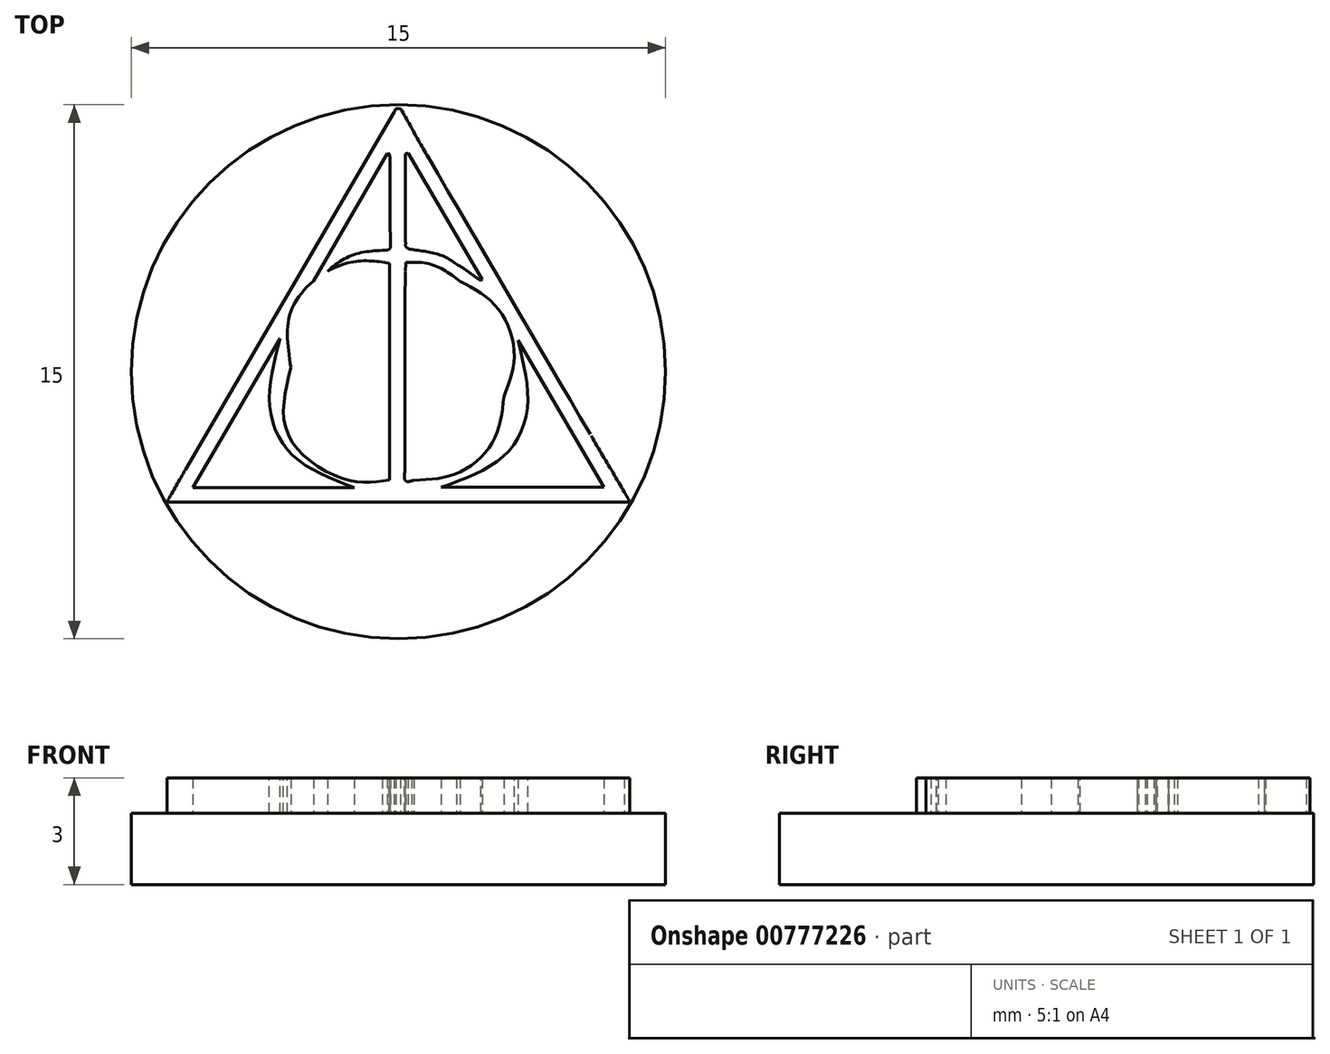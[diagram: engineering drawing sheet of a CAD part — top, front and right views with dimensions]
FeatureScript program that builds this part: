
annotation { "Feature Type Name" : "Feature", "Feature Type Description" : "" }
export const myFeature = defineFeature(function(context is Context, id is Id, definition is map)
    precondition{}
    {
        {
            var Q0;
            Q0=qCreatedBy(makeId("Top.planeOp"),FACE);
            var sketch = newSketch(context, id + "F0", { "sketchPlane" : qUnion([Q0])});
            skCircle(sketch, "E0", {"center": v(0, 0) * mm, "radius": 7.5 * mm});
            skSolve(sketch);
        }
        {
            var Q0;
            Q0=qCreatedBy(makeId("Top.planeOp"),FACE);
            var sketch = newSketch(context, id + "F1", { "sketchPlane" : qUnion([Q0])});
            skFitSpline(sketch, "E1", {"points": [v(2.32, 2.56) * mm, v(2.33, 2.57) * mm, v(2.35, 2.58) * mm, v(2.36, 2.59) * mm]});
            skFitSpline(sketch, "E2", {"points": [v(2.36, 2.59) * mm, v(1.66, 3.77) * mm, v(0.97, 4.96) * mm, v(0.27, 6.15) * mm]});
            skFitSpline(sketch, "E3", {"points": [v(0.27, 6.15) * mm, v(0.25, 6.14) * mm, v(0.22, 6.13) * mm, v(0.2, 6.12) * mm]});
            skFitSpline(sketch, "E4", {"points": [v(0.2, 6.12) * mm, v(0.2, 5.27) * mm, v(0.2, 4.43) * mm, v(0.2, 3.58) * mm]});
            skFitSpline(sketch, "E5", {"points": [v(0.2, 3.58) * mm, v(0.2, 3.53) * mm, v(0.3, 3.44) * mm, v(0.37, 3.43) * mm]});
            skFitSpline(sketch, "E6", {"points": [v(0.37, 3.43) * mm, v(0.82, 3.37) * mm, v(1.25, 3.25) * mm, v(1.64, 3.02) * mm]});
            skFitSpline(sketch, "E7", {"points": [v(1.64, 3.02) * mm, v(1.87, 2.88) * mm, v(2.1, 2.71) * mm, v(2.32, 2.56) * mm]});
            skFitSpline(sketch, "E8", {"points": [v(-2.4, 2.54) * mm, v(-2.37, 2.53) * mm, v(-2.36, 2.52) * mm, v(-2.34, 2.5) * mm]});
            skFitSpline(sketch, "E9", {"points": [v(-2.34, 2.5) * mm, v(-2.31, 2.53) * mm, v(-2.28, 2.54) * mm, v(-2.25, 2.57) * mm]});
            skFitSpline(sketch, "E10", {"points": [v(-2.25, 2.57) * mm, v(-1.74, 3.03) * mm, v(-1.14, 3.32) * mm, v(-0.45, 3.41) * mm]});
            skFitSpline(sketch, "E11", {"points": [v(-0.45, 3.41) * mm, v(-0.27, 3.43) * mm, v(-0.23, 3.5) * mm, v(-0.23, 3.67) * mm]});
            skFitSpline(sketch, "E12", {"points": [v(-0.23, 3.67) * mm, v(-0.23, 4.43) * mm, v(-0.23, 5.19) * mm, v(-0.23, 5.94) * mm]});
            skFitSpline(sketch, "E13", {"points": [v(-0.23, 5.94) * mm, v(-0.23, 6) * mm, v(-0.25, 6.07) * mm, v(-0.26, 6.13) * mm]});
            skFitSpline(sketch, "E14", {"points": [v(-0.26, 6.13) * mm, v(-0.27, 6.13) * mm, v(-0.3, 6.13) * mm, v(-0.3, 6.13) * mm]});
            skFitSpline(sketch, "E15", {"points": [v(-0.3, 6.13) * mm, v(-1, 4.94) * mm, v(-1.7, 3.74) * mm, v(-2.4, 2.54) * mm]});
            skFitSpline(sketch, "E16", {"points": [v(3.35, 0.88) * mm, v(3.62, -1) * mm, v(2.94, -2.38) * mm, v(1.2, -3.25) * mm]});
            skFitSpline(sketch, "E17", {"points": [v(1.2, -3.25) * mm, v(2.75, -3.25) * mm, v(4.24, -3.25) * mm, v(5.77, -3.25) * mm]});
            skFitSpline(sketch, "E18", {"points": [v(5.77, -3.25) * mm, v(4.95, -1.84) * mm, v(4.15, -0.48) * mm, v(3.35, 0.88) * mm]});
            skFitSpline(sketch, "E19", {"points": [v(-5.78, -3.25) * mm, v(-4.22, -3.25) * mm, v(-2.73, -3.25) * mm, v(-1.25, -3.25) * mm]});
            skFitSpline(sketch, "E20", {"points": [v(-1.25, -3.25) * mm, v(-2.96, -2.35) * mm, v(-3.61, -0.95) * mm, v(-3.33, 0.94) * mm]});
            skFitSpline(sketch, "E21", {"points": [v(-3.33, 0.94) * mm, v(-4.13, -0.44) * mm, v(-4.94, -1.82) * mm, v(-5.78, -3.25) * mm]});
            skFitSpline(sketch, "E22", {"points": [v(-0.25, 3.05) * mm, v(-1.5, 3.03) * mm, v(-2.96, 1.85) * mm, v(-3.02, 0.13) * mm]});
            skFitSpline(sketch, "E23", {"points": [v(-3.02, 0.13) * mm, v(-3.09, -1.78) * mm, v(-1.5, -3.02) * mm, v(-0.25, -3.04) * mm]});
            skFitSpline(sketch, "E24", {"points": [v(-0.25, -3.04) * mm, v(-0.25, -1) * mm, v(-0.25, 1.02) * mm, v(-0.25, 3.05) * mm]});
            skFitSpline(sketch, "E25", {"points": [v(0.21, 3.07) * mm, v(0.2, 2.96) * mm, v(0.2, 2.86) * mm, v(0.19, 2.77) * mm]});
            skFitSpline(sketch, "E26", {"points": [v(0.19, 2.77) * mm, v(0.19, 0.9) * mm, v(0.18, -0.96) * mm, v(0.18, -2.82) * mm]});
            skFitSpline(sketch, "E27", {"points": [v(0.18, -2.82) * mm, v(0.18, -3.02) * mm, v(0.23, -3.08) * mm, v(0.43, -3.05) * mm]});
            skFitSpline(sketch, "E28", {"points": [v(0.43, -3.05) * mm, v(1.69, -2.83) * mm, v(2.67, -1.93) * mm, v(2.96, -0.7) * mm]});
            skFitSpline(sketch, "E29", {"points": [v(2.96, -0.7) * mm, v(3.25, 0.52) * mm, v(2.77, 1.8) * mm, v(1.73, 2.54) * mm]});
            skFitSpline(sketch, "E30", {"points": [v(1.73, 2.54) * mm, v(1.28, 2.86) * mm, v(0.79, 3.05) * mm, v(0.21, 3.07) * mm]});
            skFitSpline(sketch, "E31", {"points": [v(0.06, 7.4) * mm, v(0.32, 6.94) * mm, v(0.57, 6.48) * mm, v(0.83, 6.03) * mm]});
            skFitSpline(sketch, "E32", {"points": [v(0.83, 6.03) * mm, v(2.36, 3.42) * mm, v(3.88, 0.81) * mm, v(5.41, -1.8) * mm]});
            skFitSpline(sketch, "E33", {"points": [v(5.41, -1.8) * mm, v(5.72, -2.33) * mm, v(6.04, -2.86) * mm, v(6.35, -3.38) * mm]});
            skFitSpline(sketch, "E34", {"points": [v(6.35, -3.38) * mm, v(6.4, -3.46) * mm, v(6.43, -3.54) * mm, v(6.5, -3.66) * mm]});
            skFitSpline(sketch, "E35", {"points": [v(6.5, -3.66) * mm, v(2.15, -3.66) * mm, v(-2.15, -3.66) * mm, v(-6.5, -3.66) * mm]});
            skFitSpline(sketch, "E36", {"points": [v(-6.5, -3.66) * mm, v(-6.31, -3.33) * mm, v(-6.15, -3.03) * mm, v(-5.98, -2.74) * mm]});
            skFitSpline(sketch, "E37", {"points": [v(-5.98, -2.74) * mm, v(-4.02, 0.6) * mm, v(-2.07, 3.95) * mm, v(-0.12, 7.3) * mm]});
            skFitSpline(sketch, "E38", {"points": [v(-0.12, 7.3) * mm, v(-0.1, 7.32) * mm, v(-0.1, 7.36) * mm, v(-0.08, 7.4) * mm]});
            skFitSpline(sketch, "E39", {"points": [v(-0.08, 7.4) * mm, v(-0.03, 7.4) * mm, v(0.02, 7.4) * mm, v(0.06, 7.4) * mm]});
            skSolve(sketch);
        }
        {
            var Q0;
            Q0 = qSketchRegion(id + "F0", true);
            extrude(context, id + "F2", {"entities" : qUnion([Q0]), "oppositeDirection" : true, "depth" : 2 * mm, "offsetDistance" : 25 * mm});
        }
        {
            var Q0;
            Q0 = qSketchRegion(id + "F1", true);
            extrude(context, id + "F3", {"entities" : qUnion([Q0]), "operationType" : NewBodyOperationType.ADD, "depth" : 1 * mm, "offsetDistance" : 25 * mm});
        }
    });
